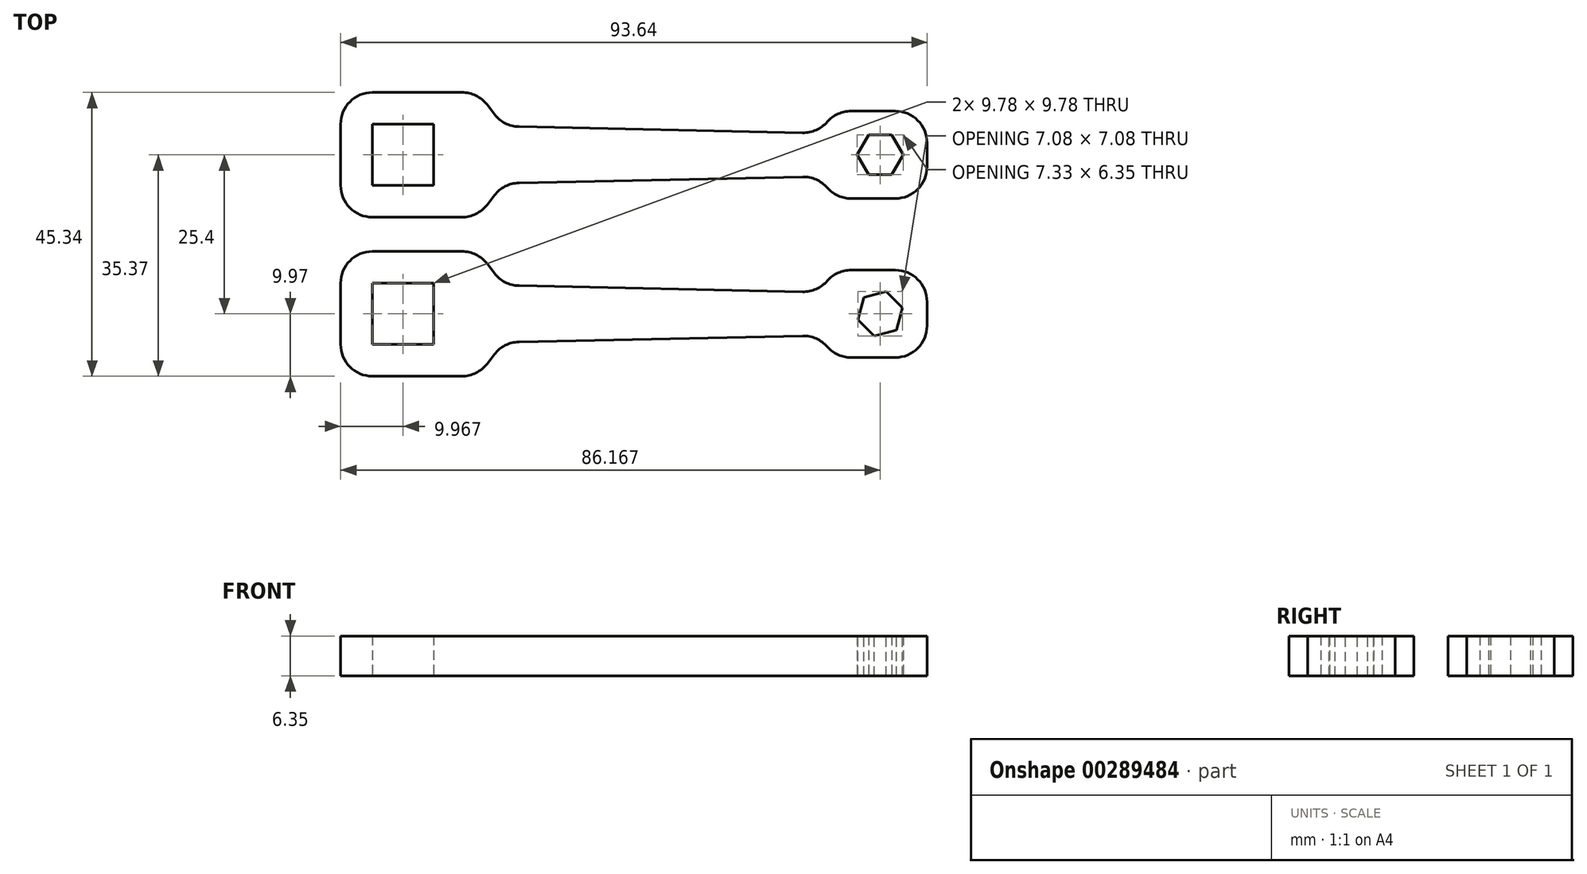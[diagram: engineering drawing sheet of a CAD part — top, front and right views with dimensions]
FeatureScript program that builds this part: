
annotation { "Feature Type Name" : "Feature", "Feature Type Description" : "" }
export const myFeature = defineFeature(function(context is Context, id is Id, definition is map)
    precondition{}
    {
        {
            var Q0;
            Q0=qCreatedBy(makeId("Top.planeOp"),FACE);
            var sketch = newSketch(context, id + "F0", { "sketchPlane" : qUnion([Q0])});
            skLineSegment(sketch, "E0.bottom", {"start": v(-24.96, 9.97) * mm, "end": v(-46.82, 9.97) * mm});
            skLineSegment(sketch, "E0.top", {"start": v(-24.96, -9.97) * mm, "end": v(-46.82, -9.97) * mm});
            skLineSegment(sketch, "E0.left", {"start": v(46.82, 6.98) * mm, "end": v(46.82, -6.98) * mm});
            skLineSegment(sketch, "E0.right", {"start": v(-46.82, 9.97) * mm, "end": v(-46.82, -9.97) * mm});
            skPoint(sketch, "E0.middle", {"position": v(0, 0) * mm});
            skCircle(sketch, "E1.cCircle", {"center": v(39.35, 0) * mm, "radius": 3.18 * mm, "construction": true});
            skLineSegment(sketch, "E1.0", {"start": v(37.51, -3.18) * mm, "end": v(35.68, 0) * mm});
            skLineSegment(sketch, "E1.1", {"start": v(35.68, 0) * mm, "end": v(37.51, 3.18) * mm});
            skLineSegment(sketch, "E1.2", {"start": v(37.51, 3.18) * mm, "end": v(41.18, 3.18) * mm});
            skLineSegment(sketch, "E1.3", {"start": v(41.18, 3.18) * mm, "end": v(43.01, 0) * mm});
            skLineSegment(sketch, "E1.4", {"start": v(43.01, 0) * mm, "end": v(41.18, -3.18) * mm});
            skLineSegment(sketch, "E1.5", {"start": v(41.18, -3.18) * mm, "end": v(37.51, -3.18) * mm});
            skPoint(sketch, "E1.0.midPoint", {"position": v(36.6, -1.59) * mm});
            skLineSegment(sketch, "E2", {"start": v(0, 0) * mm, "end": v(46.82, 0) * mm, "construction": true});
            skCircle(sketch, "E3.cCircle", {"center": v(-36.85, 0) * mm, "radius": 4.89 * mm, "construction": true});
            skLineSegment(sketch, "E3.0", {"start": v(-41.74, 4.89) * mm, "end": v(-31.96, 4.89) * mm});
            skLineSegment(sketch, "E3.1", {"start": v(-31.96, 4.89) * mm, "end": v(-31.96, -4.89) * mm});
            skLineSegment(sketch, "E3.2", {"start": v(-31.96, -4.89) * mm, "end": v(-41.74, -4.89) * mm});
            skLineSegment(sketch, "E3.3", {"start": v(-41.74, -4.89) * mm, "end": v(-41.74, 4.89) * mm});
            skPoint(sketch, "E3.0.midPoint", {"position": v(-36.85, 4.89) * mm});
            skLineSegment(sketch, "E4", {"start": v(46.82, 6.99) * mm, "end": v(31.87, 6.99) * mm});
            skLineSegment(sketch, "E5.MirrorCS", {"start": v(46.82, -6.98) * mm, "end": v(31.87, -6.99) * mm});
            skPoint(sketch, "E6.orphan", {"position": v(46.82, 9.97) * mm});
            skPoint(sketch, "E7.orphan", {"position": v(46.82, -9.97) * mm});
            skLineSegment(sketch, "E8", {"start": v(37.51, -3.18) * mm, "end": v(-36.85, -4.89) * mm, "construction": true});
            skLineSegment(sketch, "E9.top", {"start": v(46.82, -6.98) * mm, "end": v(31.87, -6.98) * mm});
            skLineSegment(sketch, "E9.left", {"start": v(46.82, 6.98) * mm, "end": v(46.82, -6.99) * mm});
            skLineSegment(sketch, "E9.right", {"start": v(31.87, 6.99) * mm, "end": v(31.87, 3.42) * mm});
            skLineSegment(sketch, "E10", {"start": v(31.87, 3.42) * mm, "end": v(-20.8, 4.54) * mm});
            skLineSegment(sketch, "E11", {"start": v(-20.8, 4.54) * mm, "end": v(-24.96, 9.97) * mm});
            skLineSegment(sketch, "E12.MirrorCS", {"start": v(-20.8, -4.54) * mm, "end": v(-24.96, -9.97) * mm});
            skLineSegment(sketch, "E13.MirrorCS", {"start": v(31.87, -3.42) * mm, "end": v(-20.8, -4.54) * mm});
            skPoint(sketch, "E14.end.orphan", {"position": v(0, 9.97) * mm});
            skPoint(sketch, "E15.orphan", {"position": v(15.07, 6.99) * mm});
            skPoint(sketch, "E16.orphan", {"position": v(15.07, -6.99) * mm});
            skPoint(sketch, "E17.orphan", {"position": v(0, -9.97) * mm});
            skLineSegment(sketch, "E18.trimOffspring", {"start": v(31.87, -3.42) * mm, "end": v(31.87, -6.99) * mm});
            skSolve(sketch);
        }
        {
            var Q0;
            Q0 = qSketchRegion(id + "F0", true);
            extrude(context, id + "F1", {"entities" : qUnion([Q0]), "depth" : 6.35 * mm, "offsetDistance" : 25.4 * mm});
        }
        {
            var Q0;
            Q0=makeQuery(id+"F1.opExtrude","SWEPT_EDGE",EDGE,{"disambiguationData":[OSD([sQuery(id+"F0.wireOp",EDGE,"E0.bottom"),sQuery(id+"F0.wireOp",EDGE,"E0.left")])]});
            var Q1;
            Q1=makeQuery(id+"F1.opExtrude","SWEPT_EDGE",EDGE,{"disambiguationData":[OSD([sQuery(id+"F0.wireOp",EDGE,"E0.top"),sQuery(id+"F0.wireOp",EDGE,"E0.left")])]});
            var Q2;
            Q2=makeQuery(id+"F1.opExtrude","SWEPT_EDGE",EDGE,{"disambiguationData":[OSD([sQuery(id+"F0.wireOp",EDGE,"E0.top"),sQuery(id+"F0.wireOp",EDGE,"E0.right")])]});
            var Q3;
            Q3=makeQuery(id+"F1.opExtrude","SWEPT_EDGE",EDGE,{"disambiguationData":[OSD([sQuery(id+"F0.wireOp",EDGE,"E0.bottom"),sQuery(id+"F0.wireOp",EDGE,"E0.right")])]});
            fillet(context, id + "F2", {"entities" : qUnion([Q0, Q1, Q2, Q3]), "radius" : 5.08 * mm, "tangentPropagation" : true, "allowEdgeOverflow" : false});
        }
        {
            var Q0;
            Q0=makeQuery(id+"F1.opExtrude","SWEPT_FACE",FACE,{"disambiguationData":[OSD([sQuery(id+"F0.wireOp",EDGE,"E3.0")])]});
            var sketch = newSketch(context, id + "F3", { "sketchPlane" : qUnion([Q0])});
            skLineSegment(sketch, "E19.0.0", {"start": v(-41.74, 0) * mm, "end": v(-31.96, 0) * mm, "construction": true});
            skLineSegment(sketch, "E19.0.1", {"start": v(-31.96, 0) * mm, "end": v(-31.96, 6.35) * mm, "construction": true});
            skLineSegment(sketch, "E19.0.2", {"start": v(-31.96, 6.35) * mm, "end": v(-41.74, 6.35) * mm, "construction": true});
            skLineSegment(sketch, "E19.0.3", {"start": v(-41.74, 6.35) * mm, "end": v(-41.74, 0) * mm, "construction": true});
            skLineSegment(sketch, "E20", {"start": v(-36.85, 6.35) * mm, "end": v(-36.85, 0) * mm, "construction": true});
            skArc(sketch, "E21", {"start": v(-36.85, 2.03) * mm, "mid": v(-35.71, 3.18) * mm, "end": v(-36.85, 4.32) * mm});
            skPoint(sketch, "E22", {"position": v(-36.85, 4.32) * mm});
            skPoint(sketch, "E23", {"position": v(-36.85, 2.03) * mm});
            skLineSegment(sketch, "E24", {"start": v(-36.85, 4.32) * mm, "end": v(-36.85, 2.03) * mm});
            skSolve(sketch);
        }
        {
            var Q0;
            Q0=makeQuery(id+"F1.opExtrude","CAP_FACE",FACE,{"disambiguationData":[OSD([sQuery(id+"F0.wireOp",EDGE,"E0.bottom"),sQuery(id+"F0.wireOp",EDGE,"E0.top"),sQuery(id+"F0.wireOp",EDGE,"E0.left"),sQuery(id+"F0.wireOp",EDGE,"E0.right"),sQuery(id+"F0.wireOp",EDGE,"E1.0"),sQuery(id+"F0.wireOp",EDGE,"E1.1"),sQuery(id+"F0.wireOp",EDGE,"E1.2"),sQuery(id+"F0.wireOp",EDGE,"E1.3"),sQuery(id+"F0.wireOp",EDGE,"E1.4"),sQuery(id+"F0.wireOp",EDGE,"E1.5"),sQuery(id+"F0.wireOp",EDGE,"E3.0"),sQuery(id+"F0.wireOp",EDGE,"E3.1"),sQuery(id+"F0.wireOp",EDGE,"E3.2"),sQuery(id+"F0.wireOp",EDGE,"E3.3"),sQuery(id+"F0.wireOp",EDGE,"E4"),sQuery(id+"F0.wireOp",EDGE,"E14"),sQuery(id+"F0.wireOp",EDGE,"E5.MirrorCS"),sQuery(id+"F0.wireOp",EDGE,"781d7365-9fdc-4b09-921b-a88634da560d0.MirrorCS")])],"isStart":false});
            var sketch = newSketch(context, id + "F4", { "sketchPlane" : qUnion([Q0])});
            skText(sketch, "E25", { "text": "Jean\'s Genius Tools", "fontName": "OpenSans-Bold.ttf"});
            skCircle(sketch, "E26", {"center": v(-18.84, -4) * mm, "radius": 0.46 * mm});
            skCircle(sketch, "E27", {"center": v(-16.15, -3.94) * mm, "radius": 0.5 * mm});
            skFitSpline(sketch, "E28", {"points": [v(-19.54, -6.46) * mm, v(-18.87, -8.37) * mm, v(-17.7, -9.33) * mm, v(-16.59, -8.63) * mm, v(-16.3, -7.96) * mm, v(-15.62, -7.14) * mm, v(-15.5, -6.2) * mm, v(-16.26, -5.76) * mm, v(-18.78, -5.76) * mm, v(-19.54, -6.46) * mm]});
            skFitSpline(sketch, "E29", {"points": [v(-18.58, -6.58) * mm, v(-18, -6.9) * mm, v(-16.62, -6.58) * mm, v(-16.88, -7.37) * mm, v(-18.08, -7.63) * mm, v(-18.58, -6.58) * mm]});
            skFitSpline(sketch, "E30", {"points": [v(-17.61, -4.47) * mm, v(-17.93, -5.23) * mm, v(-17.5, -5.35) * mm, v(-17.61, -4.47) * mm]});
            const initialGuessF4  = {"E25": [-0.02569, -0.00186, 1, 0, 0.0038]};
            skSetInitialGuess(sketch, initialGuessF4);
            skSolve(sketch);
        }
        {
            var Q0;
            Q0=makeQuery(id+"F1.opExtrude","SWEPT_BODY",BODY,{"disambiguationData":[OSD([sQuery(id+"F0.wireOp",EDGE,"E0.bottom"),sQuery(id+"F0.wireOp",EDGE,"E0.top"),sQuery(id+"F0.wireOp",EDGE,"E0.left"),sQuery(id+"F0.wireOp",EDGE,"E0.right"),sQuery(id+"F0.wireOp",EDGE,"E1.0"),sQuery(id+"F0.wireOp",EDGE,"E1.1"),sQuery(id+"F0.wireOp",EDGE,"E1.2"),sQuery(id+"F0.wireOp",EDGE,"E1.3"),sQuery(id+"F0.wireOp",EDGE,"E1.4"),sQuery(id+"F0.wireOp",EDGE,"E1.5"),sQuery(id+"F0.wireOp",EDGE,"E3.0"),sQuery(id+"F0.wireOp",EDGE,"E3.1"),sQuery(id+"F0.wireOp",EDGE,"E3.2"),sQuery(id+"F0.wireOp",EDGE,"E3.3"),sQuery(id+"F0.wireOp",EDGE,"E4"),sQuery(id+"F0.wireOp",EDGE,"E14"),sQuery(id+"F0.wireOp",EDGE,"E5.MirrorCS"),sQuery(id+"F0.wireOp",EDGE,"781d7365-9fdc-4b09-921b-a88634da560d0.MirrorCS")])]});
            var Q1;
            Q1=qCreatedBy(makeId("Front.planeOp"),FACE);
            transform(context, id + "F5", {"entities" : qUnion([Q0]), "transformType" : TransformType.TRANSLATION_DISTANCE, "transformDirection" : qUnion([Q1]), "distance" : 25.4 * mm, "makeCopy" : true});
        }
        {
            var Q0;
            Q0=qCreatedBy(makeId("Top.planeOp"),FACE);
            var sketch = newSketch(context, id + "F6", { "sketchPlane" : qUnion([Q0])});
            skLineSegment(sketch, "E31.0", {"start": v(37.51, -22.23) * mm, "end": v(41.18, -22.23) * mm});
            skLineSegment(sketch, "E32.0", {"start": v(35.68, -25.4) * mm, "end": v(37.51, -22.23) * mm});
            skLineSegment(sketch, "E33.0", {"start": v(37.51, -28.58) * mm, "end": v(35.68, -25.4) * mm});
            skLineSegment(sketch, "E34.0", {"start": v(41.18, -28.58) * mm, "end": v(37.51, -28.58) * mm});
            skLineSegment(sketch, "E35.0", {"start": v(43.01, -25.4) * mm, "end": v(41.18, -28.58) * mm});
            skLineSegment(sketch, "E36.0", {"start": v(41.18, -22.23) * mm, "end": v(43.01, -25.4) * mm});
            skSolve(sketch);
        }
        {
            var Q0;
            Q0 = qSketchRegion(id + "F6", true);
            var Q1;
            {var subQ0=sQuery(id+"F0.wireOp",EDGE,"781d7365-9fdc-4b09-921b-a88634da560d0.MirrorCS");var subQ1=sQuery(id+"F0.wireOp",EDGE,"E5.MirrorCS");var subQ2=sQuery(id+"F0.wireOp",EDGE,"E3.3");var subQ3=sQuery(id+"F0.wireOp",EDGE,"E3.2");var subQ4=sQuery(id+"F0.wireOp",EDGE,"E3.1");var subQ5=sQuery(id+"F0.wireOp",EDGE,"E3.0");var subQ6=sQuery(id+"F0.wireOp",EDGE,"E1.5");var subQ7=sQuery(id+"F0.wireOp",EDGE,"E1.4");var subQ8=sQuery(id+"F0.wireOp",EDGE,"E1.3");var subQ9=sQuery(id+"F0.wireOp",EDGE,"E1.2");var subQ10=sQuery(id+"F0.wireOp",EDGE,"E1.1");var subQ11=sQuery(id+"F0.wireOp",EDGE,"E1.0");var subQ12=sQuery(id+"F0.wireOp",EDGE,"E0.right");var subQ13=sQuery(id+"F0.wireOp",EDGE,"E0.left");var subQ14=sQuery(id+"F0.wireOp",EDGE,"E4");var subQ15=sQuery(id+"F0.wireOp",EDGE,"E0.top");var subQ16=sQuery(id+"F0.wireOp",EDGE,"E0.bottom");var subQ17=sQuery(id+"F0.wireOp",EDGE,"E14");Q1=makeQuery(id+"F5.opPattern","COPY",FACE,{"derivedFrom":makeQuery(id+"FWteRHWmLUN65tP_1.boolean.opBoolean","SPLIT",FACE,{"disambiguationData":[TD([makeQuery(id+"F1.opExtrude","SWEPT_FACE",FACE,{"disambiguationData":[OSD([subQ16])]})])],"derivedFrom":makeQuery(id+"F1.opExtrude","CAP_FACE",FACE,{"disambiguationData":[OSD([subQ16,subQ15,subQ13,subQ12,subQ11,subQ10,subQ9,subQ8,subQ7,subQ6,subQ5,subQ4,subQ3,subQ2,subQ14,subQ17,subQ1,subQ0])],"isStart":false})}),"instanceName":"1"});}
            extrude(context, id + "F7", {"entities" : qUnion([Q0]), "operationType" : NewBodyOperationType.ADD, "endBound" : BoundingType.UP_TO_SURFACE, "depth" : 25.4 * mm, "endBoundEntityFace" : qUnion([Q1]), "offsetDistance" : 25.4 * mm});
        }
        {
            var Q0;
            {var subQ0=sQuery(id+"F0.wireOp",EDGE,"781d7365-9fdc-4b09-921b-a88634da560d0.MirrorCS");var subQ1=sQuery(id+"F0.wireOp",EDGE,"E5.MirrorCS");var subQ2=sQuery(id+"F0.wireOp",EDGE,"E3.3");var subQ3=sQuery(id+"F0.wireOp",EDGE,"E3.2");var subQ4=sQuery(id+"F0.wireOp",EDGE,"E3.1");var subQ5=sQuery(id+"F0.wireOp",EDGE,"E3.0");var subQ6=sQuery(id+"F0.wireOp",EDGE,"E1.5");var subQ7=sQuery(id+"F0.wireOp",EDGE,"E1.4");var subQ8=sQuery(id+"F0.wireOp",EDGE,"E1.3");var subQ9=sQuery(id+"F0.wireOp",EDGE,"E1.2");var subQ10=sQuery(id+"F0.wireOp",EDGE,"E1.1");var subQ11=sQuery(id+"F0.wireOp",EDGE,"E1.0");var subQ12=sQuery(id+"F0.wireOp",EDGE,"E0.right");var subQ13=sQuery(id+"F0.wireOp",EDGE,"E0.left");var subQ14=sQuery(id+"F0.wireOp",EDGE,"E4");var subQ15=sQuery(id+"F0.wireOp",EDGE,"E0.top");var subQ16=sQuery(id+"F0.wireOp",EDGE,"E0.bottom");var subQ17=sQuery(id+"F0.wireOp",EDGE,"E14");Q0=makeQuery(id+"F7.boolean.opBoolean","MERGE",FACE,{"derivedFrom":[makeQuery(id+"F5.opPattern","COPY",FACE,{"derivedFrom":makeQuery(id+"FWteRHWmLUN65tP_1.boolean.opBoolean","SPLIT",FACE,{"disambiguationData":[TD([makeQuery(id+"F1.opExtrude","SWEPT_FACE",FACE,{"disambiguationData":[OSD([subQ16])]})])],"derivedFrom":makeQuery(id+"F1.opExtrude","CAP_FACE",FACE,{"disambiguationData":[OSD([subQ16,subQ15,subQ13,subQ12,subQ11,subQ10,subQ9,subQ8,subQ7,subQ6,subQ5,subQ4,subQ3,subQ2,subQ14,subQ17,subQ1,subQ0])],"isStart":false})}),"instanceName":"1"}),makeQuery(id+"F7.opExtrude","CAP_FACE",FACE,{"disambiguationData":[OSD([sQuery(id+"F6.wireOp",EDGE,"E31.0"),sQuery(id+"F6.wireOp",EDGE,"E32.0"),sQuery(id+"F6.wireOp",EDGE,"E33.0"),sQuery(id+"F6.wireOp",EDGE,"E34.0"),sQuery(id+"F6.wireOp",EDGE,"E35.0"),sQuery(id+"F6.wireOp",EDGE,"E36.0")])],"isStart":false})]});}
            var sketch = newSketch(context, id + "F8", { "sketchPlane" : qUnion([Q0])});
            skLineSegment(sketch, "E37", {"start": v(-51.33, -12.7) * mm, "end": v(62.87, -12.7) * mm, "construction": true});
            skPoint(sketch, "E38.0", {"position": v(39.35, 0) * mm});
            skPoint(sketch, "E39.MirrorP", {"position": v(39.35, -25.4) * mm});
            skCircle(sketch, "E40.cCircle", {"center": v(39.35, -25.4) * mm, "radius": 3.18 * mm, "construction": true});
            skLineSegment(sketch, "E40.0", {"start": v(36.75, -22.8) * mm, "end": v(40.3, -21.86) * mm});
            skLineSegment(sketch, "E40.1", {"start": v(40.3, -21.86) * mm, "end": v(42.89, -24.45) * mm});
            skLineSegment(sketch, "E40.2", {"start": v(42.89, -24.45) * mm, "end": v(41.94, -28) * mm});
            skLineSegment(sketch, "E40.3", {"start": v(41.94, -28) * mm, "end": v(38.4, -28.94) * mm});
            skLineSegment(sketch, "E40.4", {"start": v(38.4, -28.94) * mm, "end": v(35.8, -26.35) * mm});
            skLineSegment(sketch, "E40.5", {"start": v(35.8, -26.35) * mm, "end": v(36.75, -22.8) * mm});
            skPoint(sketch, "E40.0.midPoint", {"position": v(38.52, -22.33) * mm});
            skLineSegment(sketch, "E41", {"start": v(39.35, -25.4) * mm, "end": v(36.35, -14.23) * mm, "construction": true});
            skLineSegment(sketch, "E42", {"start": v(39.35, -25.4) * mm, "end": v(39.35, -18.41) * mm, "construction": true});
            skSolve(sketch);
        }
        {
            var Q0;
            Q0 = qSketchRegion(id + "F8", true);
            extrude(context, id + "F9", {"entities" : qUnion([Q0]), "operationType" : NewBodyOperationType.REMOVE, "oppositeDirection" : true, "depth" : 25.4 * mm, "offsetDistance" : 25.4 * mm});
        }
        {
            var Q0;
            Q0=makeQuery(id+"F1.opExtrude","SWEPT_EDGE",EDGE,{"disambiguationData":[OSD([sQuery(id+"F0.wireOp",EDGE,"E9.right"),sQuery(id+"F0.wireOp",EDGE,"E10")])]});
            var Q1;
            Q1=makeQuery(id+"F1.opExtrude","SWEPT_EDGE",EDGE,{"disambiguationData":[OSD([sQuery(id+"F0.wireOp",EDGE,"E13.MirrorCS"),sQuery(id+"F0.wireOp",EDGE,"E18.trimOffspring")])]});
            var Q2;
            Q2=makeQuery(id+"F1.opExtrude","SWEPT_EDGE",EDGE,{"disambiguationData":[OSD([sQuery(id+"F0.wireOp",EDGE,"E12.MirrorCS"),sQuery(id+"F0.wireOp",EDGE,"E13.MirrorCS")])]});
            var Q3;
            Q3=makeQuery(id+"F1.opExtrude","SWEPT_EDGE",EDGE,{"disambiguationData":[OSD([sQuery(id+"F0.wireOp",EDGE,"E10"),sQuery(id+"F0.wireOp",EDGE,"E11")])]});
            var Q4;
            Q4=makeQuery(id+"F1.opExtrude","SWEPT_EDGE",EDGE,{"disambiguationData":[OSD([sQuery(id+"F0.wireOp",EDGE,"E4"),sQuery(id+"F0.wireOp",EDGE,"E9.left")])]});
            var Q5;
            Q5=makeQuery(id+"F1.opExtrude","SWEPT_EDGE",EDGE,{"disambiguationData":[OSD([sQuery(id+"F0.wireOp",EDGE,"E9.top"),sQuery(id+"F0.wireOp",EDGE,"E9.left")])]});
            fillet(context, id + "F10", {"entities" : qUnion([Q0, Q1, Q2, Q3, Q4, Q5]), "tangentPropagation" : true, "radius" : 5.08 * mm, "defaultsChanged" : false, "vertexSettings" : [], "allowEdgeOverflow" : false});
        }
        {
            var Q0;
            Q0=makeQuery(id+"F10.opFillet","BLEND_EDGE",EDGE,{"blendedFrom":[makeQuery(id+"F1.opExtrude","SWEPT_EDGE",EDGE,{"disambiguationData":[OSD([sQuery(id+"F0.wireOp",EDGE,"E13.MirrorCS"),sQuery(id+"F0.wireOp",EDGE,"E18.trimOffspring")])]}),makeQuery(id+"F1.opExtrude","SWEPT_FACE",FACE,{"disambiguationData":[OSD([sQuery(id+"F0.wireOp",EDGE,"E9.top")])]})],"blendedInto":[makeQuery(id+"F1.opExtrude","SWEPT_FACE",FACE,{"disambiguationData":[OSD([sQuery(id+"F0.wireOp",EDGE,"E9.top")])]})]});
            var Q1;
            Q1=makeQuery(id+"F10.opFillet","BLEND_EDGE",EDGE,{"blendedFrom":[makeQuery(id+"F1.opExtrude","SWEPT_EDGE",EDGE,{"disambiguationData":[OSD([sQuery(id+"F0.wireOp",EDGE,"E9.right"),sQuery(id+"F0.wireOp",EDGE,"E10")])]}),makeQuery(id+"F1.opExtrude","SWEPT_FACE",FACE,{"disambiguationData":[OSD([sQuery(id+"F0.wireOp",EDGE,"E4")])]})],"blendedInto":[makeQuery(id+"F1.opExtrude","SWEPT_FACE",FACE,{"disambiguationData":[OSD([sQuery(id+"F0.wireOp",EDGE,"E4")])]})]});
            var Q2;
            Q2=makeQuery(id+"F5.opPattern","COPY",EDGE,{"derivedFrom":makeQuery(id+"F1.opExtrude","SWEPT_EDGE",EDGE,{"disambiguationData":[OSD([sQuery(id+"F0.wireOp",EDGE,"E4"),sQuery(id+"F0.wireOp",EDGE,"E9.left")])]}),"instanceName":"1"});
            var Q3;
            Q3=makeQuery(id+"F5.opPattern","COPY",EDGE,{"derivedFrom":makeQuery(id+"F1.opExtrude","SWEPT_EDGE",EDGE,{"disambiguationData":[OSD([sQuery(id+"F0.wireOp",EDGE,"E9.top"),sQuery(id+"F0.wireOp",EDGE,"E9.left")])]}),"instanceName":"1"});
            var Q4;
            Q4=makeQuery(id+"F5.opPattern","COPY",EDGE,{"derivedFrom":makeQuery(id+"F1.opExtrude","SWEPT_EDGE",EDGE,{"disambiguationData":[OSD([sQuery(id+"F0.wireOp",EDGE,"E10"),sQuery(id+"F0.wireOp",EDGE,"E11")])]}),"instanceName":"1"});
            var Q5;
            Q5=makeQuery(id+"F5.opPattern","COPY",EDGE,{"derivedFrom":makeQuery(id+"F1.opExtrude","SWEPT_EDGE",EDGE,{"disambiguationData":[OSD([sQuery(id+"F0.wireOp",EDGE,"E12.MirrorCS"),sQuery(id+"F0.wireOp",EDGE,"E13.MirrorCS")])]}),"instanceName":"1"});
            fillet(context, id + "F11", {"entities" : qUnion([Q0, Q1, Q2, Q3, Q4, Q5]), "tangentPropagation" : true, "radius" : 5.08 * mm, "defaultsChanged" : false, "vertexSettings" : [], "allowEdgeOverflow" : false});
        }
        {
            var Q0;
            Q0=makeQuery(id+"F5.opPattern","COPY",EDGE,{"derivedFrom":makeQuery(id+"F1.opExtrude","SWEPT_EDGE",EDGE,{"disambiguationData":[OSD([sQuery(id+"F0.wireOp",EDGE,"E13.MirrorCS"),sQuery(id+"F0.wireOp",EDGE,"E18.trimOffspring")])]}),"instanceName":"1"});
            var Q1;
            Q1=makeQuery(id+"F5.opPattern","COPY",EDGE,{"derivedFrom":makeQuery(id+"F1.opExtrude","SWEPT_EDGE",EDGE,{"disambiguationData":[OSD([sQuery(id+"F0.wireOp",EDGE,"E9.right"),sQuery(id+"F0.wireOp",EDGE,"E10")])]}),"instanceName":"1"});
            fillet(context, id + "F12", {"entities" : qUnion([Q0, Q1]), "tangentPropagation" : true, "radius" : 5.08 * mm, "defaultsChanged" : false, "vertexSettings" : [], "allowEdgeOverflow" : false});
        }
        {
            var Q0;
            Q0=makeQuery(id+"F12.opFillet","BLEND_EDGE",EDGE,{"blendedFrom":[makeQuery(id+"F5.opPattern","COPY",EDGE,{"derivedFrom":makeQuery(id+"F1.opExtrude","SWEPT_EDGE",EDGE,{"disambiguationData":[OSD([sQuery(id+"F0.wireOp",EDGE,"E9.right"),sQuery(id+"F0.wireOp",EDGE,"E10")])]}),"instanceName":"1"}),makeQuery(id+"F5.opPattern","COPY",FACE,{"derivedFrom":makeQuery(id+"F1.opExtrude","SWEPT_FACE",FACE,{"disambiguationData":[OSD([sQuery(id+"F0.wireOp",EDGE,"E4")])]}),"instanceName":"1"})],"blendedInto":[makeQuery(id+"F5.opPattern","COPY",FACE,{"derivedFrom":makeQuery(id+"F1.opExtrude","SWEPT_FACE",FACE,{"disambiguationData":[OSD([sQuery(id+"F0.wireOp",EDGE,"E4")])]}),"instanceName":"1"})]});
            var Q1;
            Q1=makeQuery(id+"F12.opFillet","BLEND_EDGE",EDGE,{"blendedFrom":[makeQuery(id+"F5.opPattern","COPY",EDGE,{"derivedFrom":makeQuery(id+"F1.opExtrude","SWEPT_EDGE",EDGE,{"disambiguationData":[OSD([sQuery(id+"F0.wireOp",EDGE,"E13.MirrorCS"),sQuery(id+"F0.wireOp",EDGE,"E18.trimOffspring")])]}),"instanceName":"1"}),makeQuery(id+"F5.opPattern","COPY",FACE,{"derivedFrom":makeQuery(id+"F1.opExtrude","SWEPT_FACE",FACE,{"disambiguationData":[OSD([sQuery(id+"F0.wireOp",EDGE,"E9.top")])]}),"instanceName":"1"})],"blendedInto":[makeQuery(id+"F5.opPattern","COPY",FACE,{"derivedFrom":makeQuery(id+"F1.opExtrude","SWEPT_FACE",FACE,{"disambiguationData":[OSD([sQuery(id+"F0.wireOp",EDGE,"E9.top")])]}),"instanceName":"1"})]});
            fillet(context, id + "F13", {"entities" : qUnion([Q0, Q1]), "tangentPropagation" : true, "radius" : 5.08 * mm, "defaultsChanged" : false, "vertexSettings" : [], "allowEdgeOverflow" : false});
        }
    });
